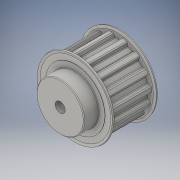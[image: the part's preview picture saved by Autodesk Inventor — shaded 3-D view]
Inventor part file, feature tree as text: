
AUTODESK INVENTOR PART (.ipt)
format: ipt  version: 2016 (Build 200138000, 138)  size: 373,248 bytes
history: native  units: in
note: dims shown in document units (in); Inventor stores cm internally (conversion verified against a paired STEP export)
features: chamfer x2, extrude x1, sketch x1, imported_body x1
ambient origin geometry x8: Origin, YZ Plane, XZ Plane, XY Plane, X Axis, Y Axis, Z Axis, Center Point
bodies: Solid1 (feature_tree)
feature tree (5):
  extrude  "Extrusion1"  Depth=1.5748in TaperAngle=0.0deg
  chamfer  "Chamfer1"  Distance=0.0098in Angle=45.0deg
  chamfer  "Chamfer2"  Distance=0.0098in Angle=45.0deg
  sketch  "Sketch1"  dims[d0=0.251in d1=1.5748in d2=0.0in d3=0.0098in d4=0.0787in d5=45.0deg d6=0.0098in d7=0.0787in d8=45.0deg]
  imported_body  "Base1"
